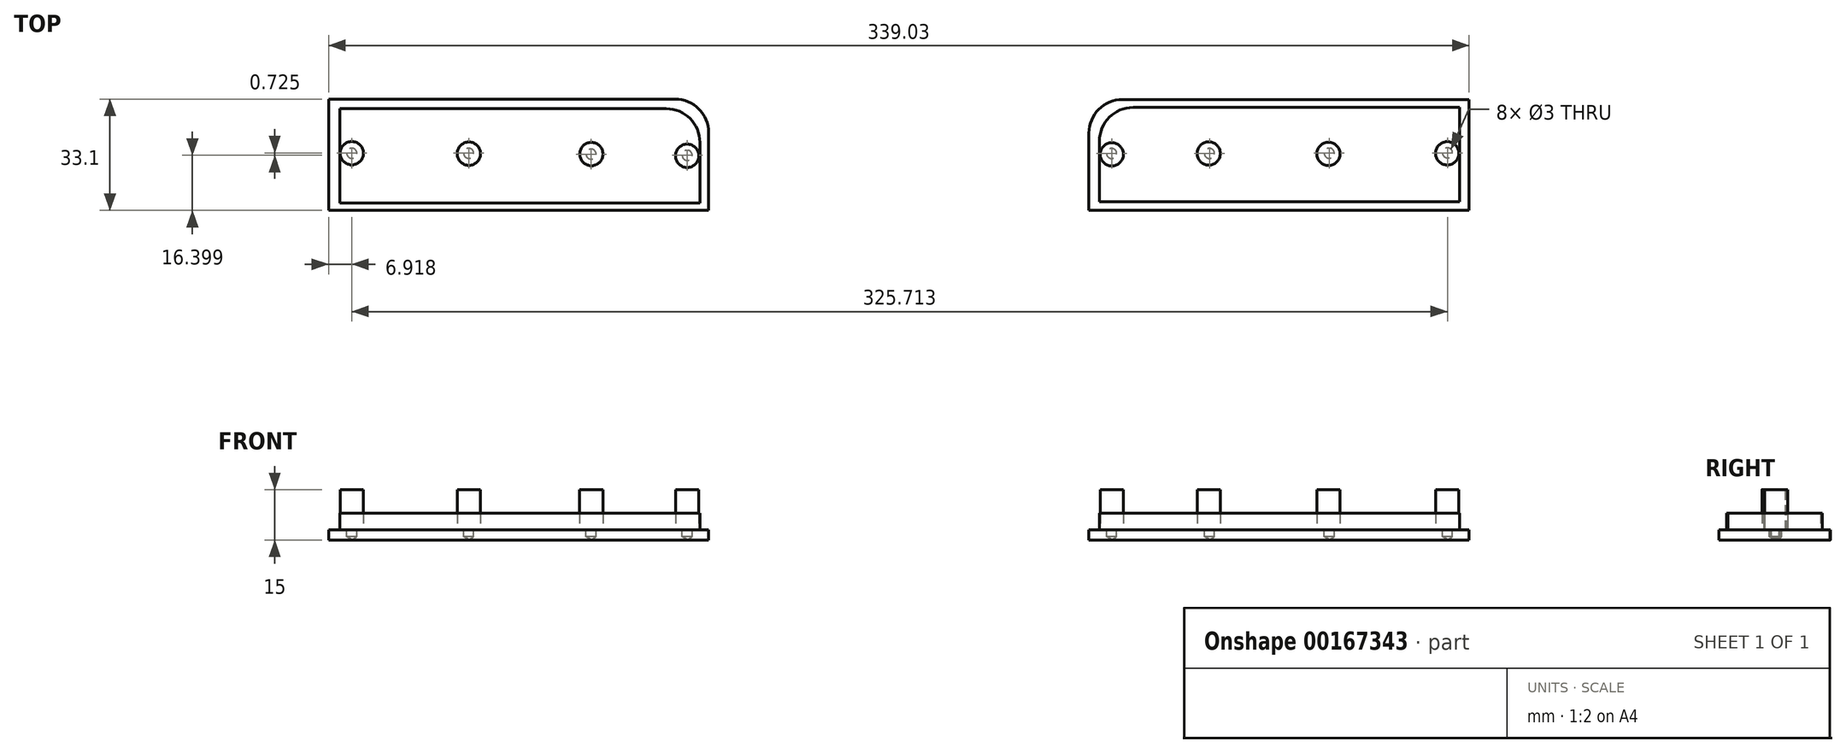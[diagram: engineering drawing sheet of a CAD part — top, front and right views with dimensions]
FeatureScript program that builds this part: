
annotation { "Feature Type Name" : "Feature", "Feature Type Description" : "" }
export const myFeature = defineFeature(function(context is Context, id is Id, definition is map)
    precondition{}
    {
        {
            var Q0;
            Q0=qCreatedBy(makeId("Top.planeOp"),FACE);
            var sketch = newSketch(context, id + "F0", { "sketchPlane" : qUnion([Q0])});
            skLineSegment(sketch, "E0.bottom", {"start": v(66.11, 78.9) * mm, "end": v(169.11, 78.9) * mm});
            skLineSegment(sketch, "E0.top", {"start": v(56.11, 45.9) * mm, "end": v(169.11, 45.9) * mm});
            skLineSegment(sketch, "E0.left", {"start": v(56.11, 68.9) * mm, "end": v(56.11, 45.9) * mm});
            skLineSegment(sketch, "E0.right", {"start": v(169.11, 78.9) * mm, "end": v(169.11, 45.9) * mm});
            skLineSegment(sketch, "E1.bottom", {"start": v(-169.92, 79) * mm, "end": v(-66.92, 79) * mm});
            skLineSegment(sketch, "E1.top", {"start": v(-169.92, 46) * mm, "end": v(-56.92, 46) * mm});
            skLineSegment(sketch, "E1.left", {"start": v(-169.92, 79) * mm, "end": v(-169.92, 46) * mm});
            skLineSegment(sketch, "E1.right", {"start": v(-56.92, 69) * mm, "end": v(-56.92, 46) * mm});
            skPoint(sketch, "E2.visualSharp", {"position": v(-56.92, 79) * mm});
            skArc(sketch, "E2.filletArc", {"start": v(-56.92, 69) * mm, "mid": v(-59.85, 76.07) * mm, "end": v(-66.92, 79) * mm});
            skPoint(sketch, "E3.visualSharp", {"position": v(56.11, 78.9) * mm});
            skArc(sketch, "E3.filletArc", {"start": v(66.11, 78.9) * mm, "mid": v(59.04, 75.97) * mm, "end": v(56.11, 68.9) * mm});
            skSolve(sketch);
        }
        {
            var Q0;
            Q0=qSketchRegion(id+"F0",true);
            extrude(context, id + "F1", {"entities" : qUnion([Q0]), "depth" : 3 * mm});
        }
        {
            var Q0;
            Q0=makeQuery(id+"F1.opExtrude","CAP_FACE",FACE,{"disambiguationData":[OSD([sQuery(id+"F0.wireOp",EDGE,"E0.bottom"),sQuery(id+"F0.wireOp",EDGE,"E0.top"),sQuery(id+"F0.wireOp",EDGE,"E0.left"),sQuery(id+"F0.wireOp",EDGE,"E0.right"),sQuery(id+"F0.wireOp",EDGE,"E3.filletArc")])],"isStart":false});
            cPlane(context, id + "F2", {"entities" : qUnion([Q0]), "cplaneType" : CPlaneType.OFFSET, "offset" : 25 * mm, "width" : 150 * mm, "height" : 150 * mm});
        }
        {
            var Q0;
            Q0=makeQuery(id+"F1.opExtrude","CAP_FACE",FACE,{"disambiguationData":[OSD([sQuery(id+"F0.wireOp",EDGE,"E1.bottom"),sQuery(id+"F0.wireOp",EDGE,"E1.top"),sQuery(id+"F0.wireOp",EDGE,"E1.left"),sQuery(id+"F0.wireOp",EDGE,"E1.right"),sQuery(id+"F0.wireOp",EDGE,"E2.filletArc")])],"isStart":false});
            cPlane(context, id + "F3", {"entities" : qUnion([Q0]), "cplaneType" : CPlaneType.OFFSET, "offset" : 0 * mm, "width" : 150 * mm, "height" : 150 * mm});
        }
        {
            var Q0;
            Q0=makeQuery(id+"F1.opExtrude","CAP_FACE",FACE,{"disambiguationData":[OSD([sQuery(id+"F0.wireOp",EDGE,"E1.bottom"),sQuery(id+"F0.wireOp",EDGE,"E1.top"),sQuery(id+"F0.wireOp",EDGE,"E1.left"),sQuery(id+"F0.wireOp",EDGE,"E1.right"),sQuery(id+"F0.wireOp",EDGE,"E2.filletArc")])],"isStart":false});
            cPlane(context, id + "F4", {"entities" : qUnion([Q0]), "cplaneType" : CPlaneType.OFFSET, "offset" : 0 * mm, "width" : 150 * mm, "height" : 150 * mm});
        }
        {
            var Q0;
            Q0=qCreatedBy(id+"F4.planeOp",FACE);
            var sketch = newSketch(context, id + "F5", { "sketchPlane" : qUnion([Q0])});
            skLineSegment(sketch, "E4.bottom", {"start": v(-166.51, 76.14) * mm, "end": v(-69.51, 76.14) * mm});
            skLineSegment(sketch, "E4.top", {"start": v(-166.51, 48.14) * mm, "end": v(-59.51, 48.14) * mm});
            skLineSegment(sketch, "E4.left", {"start": v(-166.51, 76.14) * mm, "end": v(-166.51, 48.14) * mm});
            skLineSegment(sketch, "E4.right", {"start": v(-59.51, 66.14) * mm, "end": v(-59.51, 48.14) * mm});
            skArc(sketch, "E5.filletArc", {"start": v(-59.51, 66.14) * mm, "mid": v(-62.44, 73.21) * mm, "end": v(-69.51, 76.14) * mm});
            skLineSegment(sketch, "E6.bottom", {"start": v(59.25, 48.54) * mm, "end": v(166.25, 48.54) * mm});
            skLineSegment(sketch, "E6.top", {"start": v(69.25, 76.54) * mm, "end": v(166.25, 76.54) * mm});
            skLineSegment(sketch, "E6.left", {"start": v(59.25, 48.54) * mm, "end": v(59.25, 66.54) * mm});
            skLineSegment(sketch, "E6.right", {"start": v(166.25, 48.54) * mm, "end": v(166.25, 76.54) * mm});
            skPoint(sketch, "E7.visualSharp", {"position": v(59.25, 76.54) * mm});
            skArc(sketch, "E7.filletArc", {"start": v(69.25, 76.54) * mm, "mid": v(62.18, 73.6) * mm, "end": v(59.25, 66.54) * mm});
            skSolve(sketch);
        }
        {
            var Q0;
            Q0=qSketchRegion(id+"F5",true);
            extrude(context, id + "F6", {"entities" : qUnion([Q0]), "depth" : 5 * mm});
        }
        {
            var Q0;
            Q0=qCreatedBy(id+"F4.planeOp",FACE);
            var sketch = newSketch(context, id + "F7", { "sketchPlane" : qUnion([Q0])});
            skCircle(sketch, "E8", {"center": v(-163, 62.9) * mm, "radius": 3.46 * mm});
            skCircle(sketch, "E9", {"center": v(-128.2, 62.78) * mm, "radius": 3.46 * mm});
            skCircle(sketch, "E10", {"center": v(-91.8, 62.66) * mm, "radius": 3.46 * mm});
            skCircle(sketch, "E11", {"center": v(-63.32, 62.14) * mm, "radius": 3.46 * mm});
            skCircle(sketch, "E12", {"center": v(62.91, 62.57) * mm, "radius": 3.46 * mm});
            skCircle(sketch, "E13", {"center": v(91.73, 62.84) * mm, "radius": 3.46 * mm});
            skCircle(sketch, "E14", {"center": v(127.32, 62.72) * mm, "radius": 3.46 * mm});
            skCircle(sketch, "E15", {"center": v(162.64, 62.89) * mm, "radius": 3.46 * mm});
            skSolve(sketch);
        }
        {
            var Q0;
            Q0=qSketchRegion(id+"F7",true);
            extrude(context, id + "F8", {"entities" : qUnion([Q0]), "depth" : 12 * mm});
        }
        {
            var Q0;
            Q0=makeQuery(id+"F8.opExtrude","CAP_FACE",FACE,{"disambiguationData":[OSD([sQuery(id+"F7.wireOp",EDGE,"E8")])],"isStart":false});
            var sketch = newSketch(context, id + "F9", { "sketchPlane" : qUnion([Q0])});
            skPoint(sketch, "E16", {"position": v(-163, 62.9) * mm});
            skPoint(sketch, "E17", {"position": v(-128.27, 62.9) * mm});
            skPoint(sketch, "E18", {"position": v(-91.88, 62.65) * mm});
            skPoint(sketch, "E19", {"position": v(-63.3, 62.3) * mm});
            skPoint(sketch, "E20", {"position": v(62.87, 62.84) * mm});
            skPoint(sketch, "E21", {"position": v(91.95, 62.84) * mm});
            skPoint(sketch, "E22", {"position": v(127.56, 62.93) * mm});
            skPoint(sketch, "E23", {"position": v(162.71, 63.02) * mm});
            skSolve(sketch);
        }
        {
            var Q0;
            Q0=sQuery(id+"F9.wireOp",VERTEX,"E16");
            var Q1;
            Q1=sQuery(id+"F9.wireOp",VERTEX,"E17");
            var Q2;
            Q2=sQuery(id+"F9.wireOp",VERTEX,"E18");
            var Q3;
            Q3=sQuery(id+"F9.wireOp",VERTEX,"E19");
            var Q4;
            Q4=sQuery(id+"F9.wireOp",VERTEX,"E20");
            var Q5;
            Q5=sQuery(id+"F9.wireOp",VERTEX,"E21");
            var Q6;
            Q6=sQuery(id+"F9.wireOp",VERTEX,"E22");
            var Q7;
            Q7=sQuery(id+"F9.wireOp",VERTEX,"E23");
            var Q8;
            Q8=makeQuery(id+"F1.opExtrude","SWEPT_BODY",BODY,{"disambiguationData":[OSD([sQuery(id+"F0.wireOp",EDGE,"E1.bottom"),sQuery(id+"F0.wireOp",EDGE,"E1.top"),sQuery(id+"F0.wireOp",EDGE,"E1.left"),sQuery(id+"F0.wireOp",EDGE,"E1.right"),sQuery(id+"F0.wireOp",EDGE,"E2.filletArc")])]});
            var Q9;
            Q9=makeQuery(id+"F1.opExtrude","SWEPT_BODY",BODY,{"disambiguationData":[OSD([sQuery(id+"F0.wireOp",EDGE,"E0.bottom"),sQuery(id+"F0.wireOp",EDGE,"E0.top"),sQuery(id+"F0.wireOp",EDGE,"E0.left"),sQuery(id+"F0.wireOp",EDGE,"E0.right"),sQuery(id+"F0.wireOp",EDGE,"E3.filletArc")])]});
            hole(context, id + "F10", {"style" : HoleStyle.SIMPLE, "endStyle" : HoleEndStyle.BLIND, "holeDiameter" : 3 * mm, "holeDepth" : 2 * mm, "locations" : qUnion([Q0, Q1, Q2, Q3, Q4, Q5, Q6, Q7]), "scope" : qUnion([Q8, Q9])});
        }
    });
